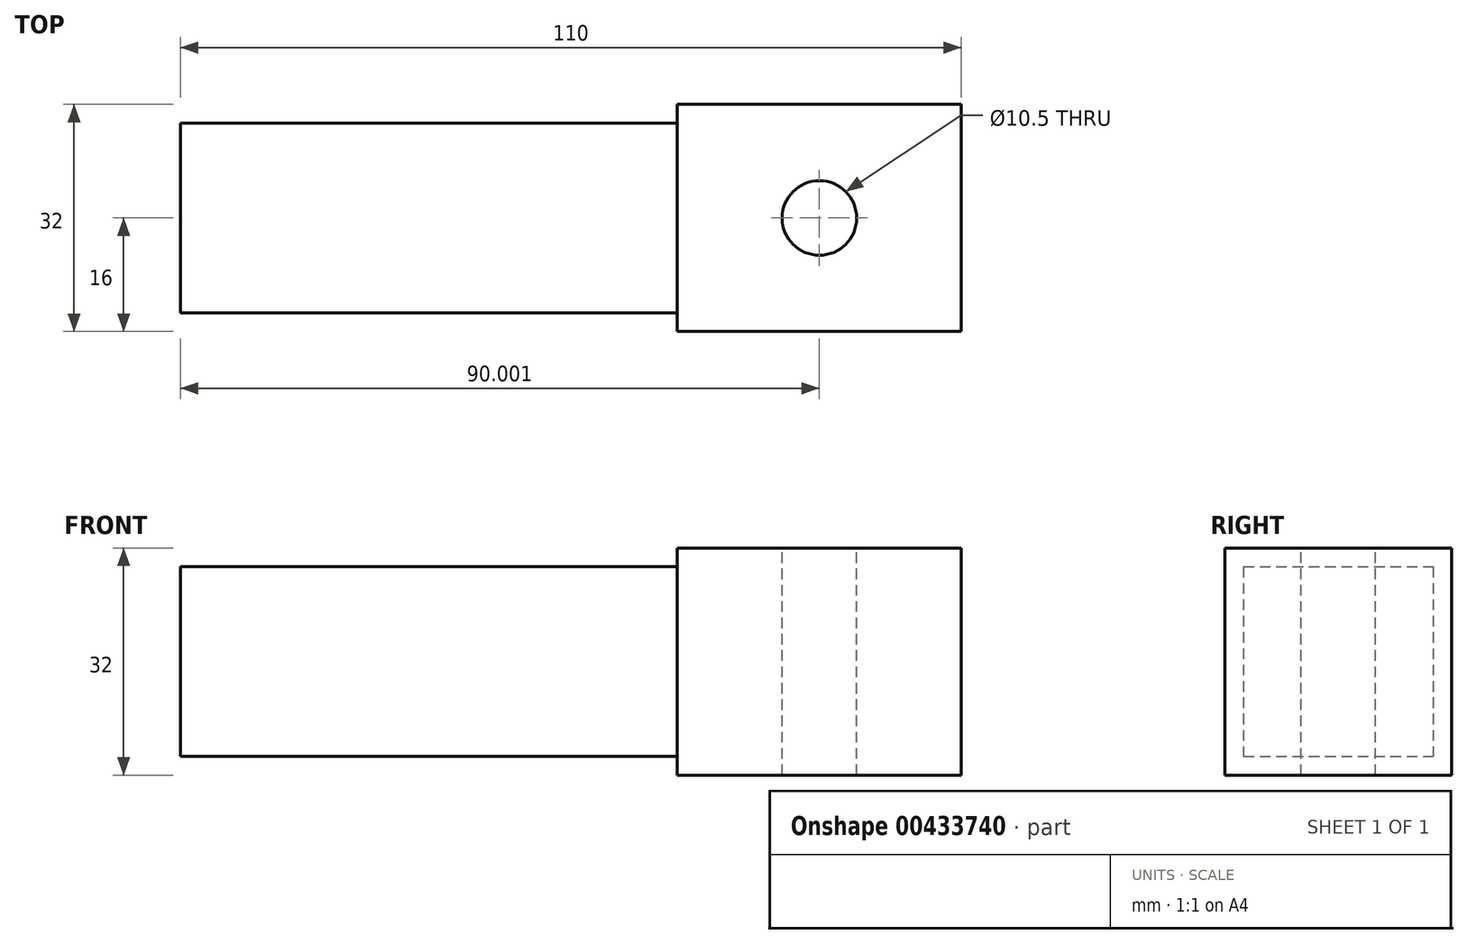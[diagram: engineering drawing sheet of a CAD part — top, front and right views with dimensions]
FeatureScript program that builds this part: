
annotation { "Feature Type Name" : "Feature", "Feature Type Description" : "" }
export const myFeature = defineFeature(function(context is Context, id is Id, definition is map)
    precondition{}
    {
        {
            var Q0;
            Q0=qCreatedBy(makeId("Front.planeOp"),FACE);
            var sketch = newSketch(context, id + "F0", { "sketchPlane" : qUnion([Q0])});
            skLineSegment(sketch, "E0.bottom", {"start": v(-49.09, 13.66) * mm, "end": v(20.91, 13.66) * mm});
            skLineSegment(sketch, "E0.top", {"start": v(-49.09, -13.04) * mm, "end": v(20.91, -13.04) * mm});
            skLineSegment(sketch, "E0.left", {"start": v(-49.09, 13.66) * mm, "end": v(-49.09, -13.04) * mm});
            skLineSegment(sketch, "E0.right", {"start": v(20.91, 13.66) * mm, "end": v(20.91, -13.04) * mm});
            skSolve(sketch);
        }
        {
            var Q0;
            Q0=qCreatedBy(makeId("Front.planeOp"),FACE);
            var sketch = newSketch(context, id + "F1", { "sketchPlane" : qUnion([Q0])});
            skLineSegment(sketch, "E1.bottom", {"start": v(20.91, 16.31) * mm, "end": v(60.91, 16.31) * mm});
            skLineSegment(sketch, "E1.top", {"start": v(20.91, -15.69) * mm, "end": v(60.91, -15.69) * mm});
            skLineSegment(sketch, "E1.left", {"start": v(20.91, 16.31) * mm, "end": v(20.91, -15.69) * mm});
            skLineSegment(sketch, "E1.right", {"start": v(60.91, 16.31) * mm, "end": v(60.91, -15.69) * mm});
            skSolve(sketch);
        }
        {
            var Q0;
            Q0 = qSketchRegion(id + "F0", true);
            extrude(context, id + "F2", {"entities" : qUnion([Q0]), "depth" : 26.7 * mm, "offsetDistance" : 25 * mm});
        }
        {
            var Q0;
            Q0 = qSketchRegion(id + "F1", true);
            extrude(context, id + "F3", {"entities" : qUnion([Q0]), "operationType" : NewBodyOperationType.ADD, "depth" : 29.35 * mm, "offsetDistance" : 25 * mm, "hasSecondDirection" : true, "secondDirectionOppositeDirection" : true, "secondDirectionDepth" : 2.65 * mm});
        }
        {
            var Q0;
            Q0=makeQuery(id+"F3.opExtrude","SWEPT_FACE",FACE,{"disambiguationData":[OSD([sQuery(id+"F1.wireOp",EDGE,"E1.bottom")])]});
            var sketch = newSketch(context, id + "F4", { "sketchPlane" : qUnion([Q0])});
            skLineSegment(sketch, "E2", {"start": v(20.91, -29.35) * mm, "end": v(20.91, 2.65) * mm});
            skCircle(sketch, "E3", {"center": v(40.91, -13.35) * mm, "radius": 5 * mm});
            skSolve(sketch);
        }
        {
            var Q0;
            Q0=sQuery(id+"F4.wireOp",VERTEX,"E3.center");
            var Q1;
            Q1=makeQuery(id+"F2.opExtrude","SWEPT_BODY",BODY,{"disambiguationData":[OSD([sQuery(id+"F0.wireOp",EDGE,"E0.bottom"),sQuery(id+"F0.wireOp",EDGE,"E0.top"),sQuery(id+"F0.wireOp",EDGE,"E0.left"),sQuery(id+"F0.wireOp",EDGE,"E0.right")])]});
            hole(context, id + "F5", {"style" : HoleStyle.SIMPLE, "endStyle" : HoleEndStyle.THROUGH, "holeDiameter" : 10.5 * mm, "majorDiameter" : 5 * mm, "isTappedThrough" : true, "tappedDepth" : 12 * mm, "tapClearance" : 3, "locations" : qUnion([Q0]), "scope" : qUnion([Q1])});
        }
    });
